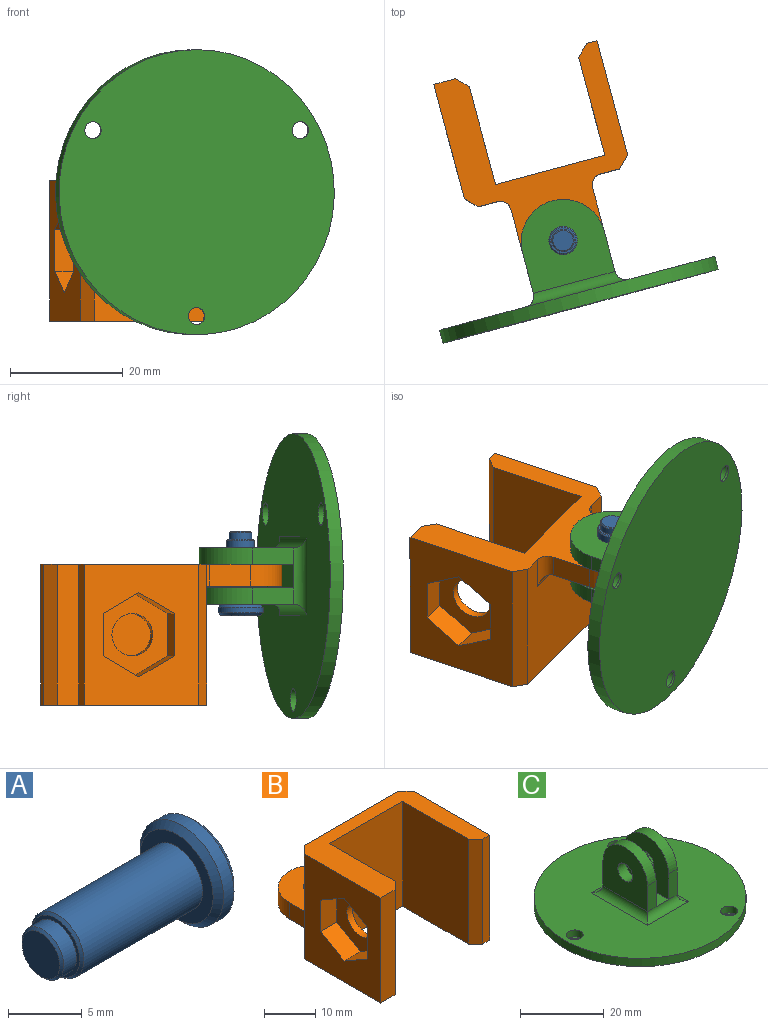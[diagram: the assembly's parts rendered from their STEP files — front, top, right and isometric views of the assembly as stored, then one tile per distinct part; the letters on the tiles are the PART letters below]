
ASSEMBLY  parts=3 mates=5
PART A: 11 faces, bbox 15x8x8 mm
  f0: plane 7x7mm, normal (-1,0,0), area 18.8mm2, adj f1,f9
  f1: cylinder r=2.5mm len=11.38mm, axis (-1,0,0), area 178.7mm2, adj f0,f7
  f2: plane 4.6x4.6mm, normal (-1,0,0), area 4.1mm2, adj f3,f7
  f3: cylinder r=2mm len=4mm, axis (-1,0,0), area 15.4mm2, adj f2,f8
  f4: plane 3.6x3.6mm, normal (-1,0,0), area 10.2mm2, adj f8
  f5: plane 7x7mm, normal (1,0,0), area 38.5mm2, adj f10
  f6: cylinder r=4mm len=8mm, axis (-1,0,0), area 25.1mm2, adj f9,f10
  f7: cone r=2.3mm half-angle=45deg, axis (1,0,0), area 4.3mm2, adj f1,f2
  f8: cone r=1.8mm half-angle=45deg, axis (1,0,0), area 3.4mm2, adj f3,f4
  f9: cone r=3.5mm half-angle=45deg, axis (1,0,0), area 16.7mm2, adj f0,f6
  f10: cone r=4mm half-angle=45deg, axis (-1,0,0), area 16.7mm2, adj f5,f6
PART B: 30 faces, bbox 30x40x25 mm
  f0: plane 26x25mm, normal (0,1,0), area 537.9mm2, adj f8,f9,f23,f24,f25,f26,f27
  f1: plane 25x4mm, normal (0,-1,0), area 100mm2, adj f7,f8,f9,f28
  f2: plane 25x18mm, normal (1,0,0), area 405.8mm2, adj f3,f8,f9,f17,f28
  f3: plane 25x20.1mm, normal (0,-1,0), area 502.5mm2, adj f2,f4,f8,f9
  f4: plane 25x18mm, normal (-1,0,0), area 450mm2, adj f3,f8,f9,f29
  f5: plane 25x1.9mm, normal (0,-1,0), area 47.5mm2, adj f6,f8,f9,f29
  f6: plane 25x21mm, normal (1,0,0), area 525mm2, adj f5,f8,f9,f26
  f7: plane 25x21mm, normal (-1,0,0), area 378.6mm2, adj f1,f8,f9,f10,f11,f12,f13,f14
  f8: plane 30x23mm, normal (0,0,1), area 280mm2, adj f0,f1,f2,f3,f4,f5,f6,f7
  f9: plane 40x30mm, normal (0,0,-1), area 492.9mm2, adj f0,f1,f2,f3,f4,f5,f6,f7
  f10: plane 6.5x4.5mm, normal (0,0.5,0.87), area 33.8mm2, adj f7,f11,f15,f16
  f11: plane 7.51x4.5mm, normal (0,1,0), area 33.8mm2, adj f7,f10,f12,f16
  f12: plane 6.5x4.5mm, normal (0,0.5,-0.87), area 33.8mm2, adj f7,f11,f13,f16
  f13: plane 6.5x4.5mm, normal (0,-0.5,-0.87), area 33.8mm2, adj f7,f12,f14,f16
  f14: plane 7.51x4.5mm, normal (0,-1,0), area 33.8mm2, adj f7,f13,f15,f16
  f15: plane 6.5x4.5mm, normal (0,-0.5,0.87), area 33.8mm2, adj f7,f10,f14,f16
  f16: plane 15.01x13mm, normal (-1,0,0), area 102.2mm2, adj f10,f11,f12,f13,f14,f15,f17
  f17: cylinder r=3.75mm len=7.5mm, axis (-1,0,0), area 35.3mm2, adj f2,f16
  f18: plane 7.5x3.9mm, normal (-1,0,0), area 29.2mm2, adj f9,f19,f21,f23
  f19: plane 15x15mm, normal (0,0,1), area 181.2mm2, adj f18,f20,f21,f22,f25
  f20: plane 7.5x3.9mm, normal (1,0,0), area 29.2mm2, adj f9,f19,f21,f24
  f21: cylinder r=7.5mm len=15mm, axis (0,0,1), area 91.9mm2, adj f9,f18,f19,f20
  f22: cylinder r=2.5mm len=5mm, axis (0,0,-1), area 61.3mm2, adj f9,f19
  f23: cylinder r=2mm len=5.9mm, axis (0,0,1), area 14.5mm2, adj f0,f9,f18,f25
  f24: cylinder r=2mm len=5.9mm, axis (0,0,-1), area 14.5mm2, adj f0,f9,f20,f25
  f25: cylinder r=2mm len=19mm, axis (1,0,0), area 51.7mm2, adj f0,f19,f23,f24
  f26: plane 25x2mm, normal (0.71,0.71,0), area 70.7mm2, adj f0,f6,f8,f9
  f27: plane 25x2mm, normal (-0.71,0.71,0), area 70.7mm2, adj f0,f7,f8,f9
  f28: plane 25x2mm, normal (0.71,-0.71,0), area 70.7mm2, adj f1,f2,f8,f9
  f29: plane 25x2mm, normal (-0.71,-0.71,0), area 70.7mm2, adj f4,f5,f8,f9
PART C: 29 faces, bbox 50.6x50.6x19.4 mm
  f0: plane 7.5x2.9mm, normal (0,1,0), area 21.8mm2, adj f18,f20,f22,f25
  f1: plane 7.5x2.9mm, normal (0,-1,0), area 21.8mm2, adj f16,f19,f21,f28
  f2: plane 15x4.2mm, normal (0,0,1), area 63mm2, adj f19,f20,f25,f28
  f3: plane 50.6x50.6mm, normal (0,0,1), area 1707.2mm2, adj f7,f10,f12,f14,f25,f26,f27,f28
  f4: cylinder r=1.5mm len=3mm, axis (0,0,1), area 3.8mm2, adj f8,f13
  f5: cylinder r=1.5mm len=3mm, axis (0,0,1), area 3.8mm2, adj f8,f11
  f6: cylinder r=1.5mm len=3mm, axis (0,0,1), area 3.8mm2, adj f8,f9
  f7: cylinder r=25.3mm len=50.6mm, axis (0,0,-1), area 381.5mm2, adj f3,f8
  f8: plane 50.6x50.6mm, normal (0,0,-1), area 1989.7mm2, adj f4,f5,f6,f7
  f9: plane 4x4mm, normal (0,0,1), area 5.5mm2, adj f6,f10
  f10: cylinder r=2mm len=4mm, axis (0,0,1), area 25.1mm2, adj f3,f9
  f11: plane 4x4mm, normal (0,0,1), area 5.5mm2, adj f5,f12
  f12: cylinder r=2mm len=4mm, axis (0,0,1), area 25.1mm2, adj f3,f11
  f13: plane 4x4mm, normal (0,0,1), area 5.5mm2, adj f4,f14
  f14: cylinder r=2mm len=4mm, axis (0,0,1), area 25.1mm2, adj f3,f13
  f15: plane 7.5x2.9mm, normal (0,1,0), area 21.8mm2, adj f16,f19,f21,f25
  f16: plane 15x15mm, normal (-1,0,0), area 181.2mm2, adj f1,f15,f21,f24,f26
  f17: plane 7.5x2.9mm, normal (0,-1,0), area 21.8mm2, adj f18,f20,f22,f28
  f18: plane 15x15mm, normal (1,0,0), area 181.2mm2, adj f0,f17,f22,f23,f27
  f19: plane 15x15mm, normal (1,0,0), area 181.2mm2, adj f1,f2,f15,f21,f24
  f20: plane 15x15mm, normal (-1,0,0), area 181.2mm2, adj f0,f2,f17,f22,f23
  f21: cylinder r=7.5mm len=15mm, axis (-1,0,0), area 68.3mm2, adj f1,f15,f16,f19
  f22: cylinder r=7.5mm len=15mm, axis (1,0,0), area 68.3mm2, adj f0,f17,f18,f20
  f23: cylinder r=2.5mm len=5mm, axis (1,0,0), area 45.6mm2, adj f18,f20
  f24: cylinder r=2.5mm len=5mm, axis (1,0,0), area 45.6mm2, adj f16,f19
  f25: cylinder r=2mm len=14mm, axis (-1,0,0), area 36mm2, adj f0,f2,f3,f15,f26,f27
  f26: cylinder r=2mm len=19mm, axis (0,-1,0), area 51.7mm2, adj f3,f16,f25,f28
  f27: cylinder r=2mm len=19mm, axis (0,1,0), area 51.7mm2, adj f3,f18,f25,f28
  f28: cylinder r=2mm len=14mm, axis (1,0,0), area 36mm2, adj f1,f2,f3,f17,f26,f27
PLACE A rot(axis=(-0.62,0.48,0.62),129deg) t=(3.08,-58.87,-47.68)mm
PLACE B rot(axis=(0.99,0.13,0),180deg) t=(-5.38,-27.28,-53.58)mm
PLACE C rot(axis=(-0.52,-0.68,-0.52),111.8deg) t=(6.21,-70.55,-55.68)mm
MATE cylindrical C.f23 <-> A.f1  axis (0,0,1) through (3.08,-58.87,-52.13)mm
MATE planar C.f16 <-> A.f1  axis (0,0,-1) through (5.08,-66.3,-60.68)mm
MATE planar C.f20 <-> B.f9  axis (0,0,-1) through (3.34,-59.83,-53.58)mm
MATE slider A.f1 <-> B.f22  axis (0,0,1) through (3.08,-58.87,-54.99)mm
MATE parallel C.f7 <-> B.f0  axis (-0.26,0.97,0) through (5.59,-68.24,-55.68)mm
